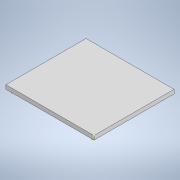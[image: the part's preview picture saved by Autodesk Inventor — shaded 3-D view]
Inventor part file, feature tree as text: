
AUTODESK INVENTOR PART (.ipt)
format: ipt  version: 2021 (Build 250183000, 183)  size: 126,976 bytes
history: native  units: mm
features: sketch x5, extrude x3, pattern_linear x3
ambient origin geometry x8: Origin, YZ Plane, XZ Plane, XY Plane, X Axis, Y Axis, Z Axis, Center Point
bodies: Solid1 (feature_tree)
feature tree (11):
  extrude  "Extrusion1"  Depth=100.0mm
  sketch  "Sketch2"  dims[d2=5.0mm d3=0.0mm d4=3.0mm]
  extrude  "Extrusion2"  Depth=3.0mm
  sketch  "Sketch4"  dims[d8=1.0mm d9=0.0mm d10=20.0mm d12=100.0mm d13=20.0mm d15=95.0mm d16=20.0mm d18=95.0mm]
  extrude  "Extrusion3"  Depth=1.0mm
  pattern_linear  "Rectangular Pattern1"  Count1=2  [1 undecoded]
  pattern_linear  "Rectangular Pattern2"  Count1=2 Spacing1=95.0mm
  pattern_linear  "Rectangular Pattern3"  Count1=2 Spacing1=95.0mm
  sketch  "Sketch1"  dims[d0=110.0mm d1=100.0mm]
  sketch  "Sketch3"  dims[d5=1.5mm d6=0.0mm d7=1.0mm]
  sketch  "Sketch5"
note: 1 required parameter value undecoded (feature->parameter linkage not recoverable at this tier; creation-order binding heuristic only, values carry confidence <= 0.55)
